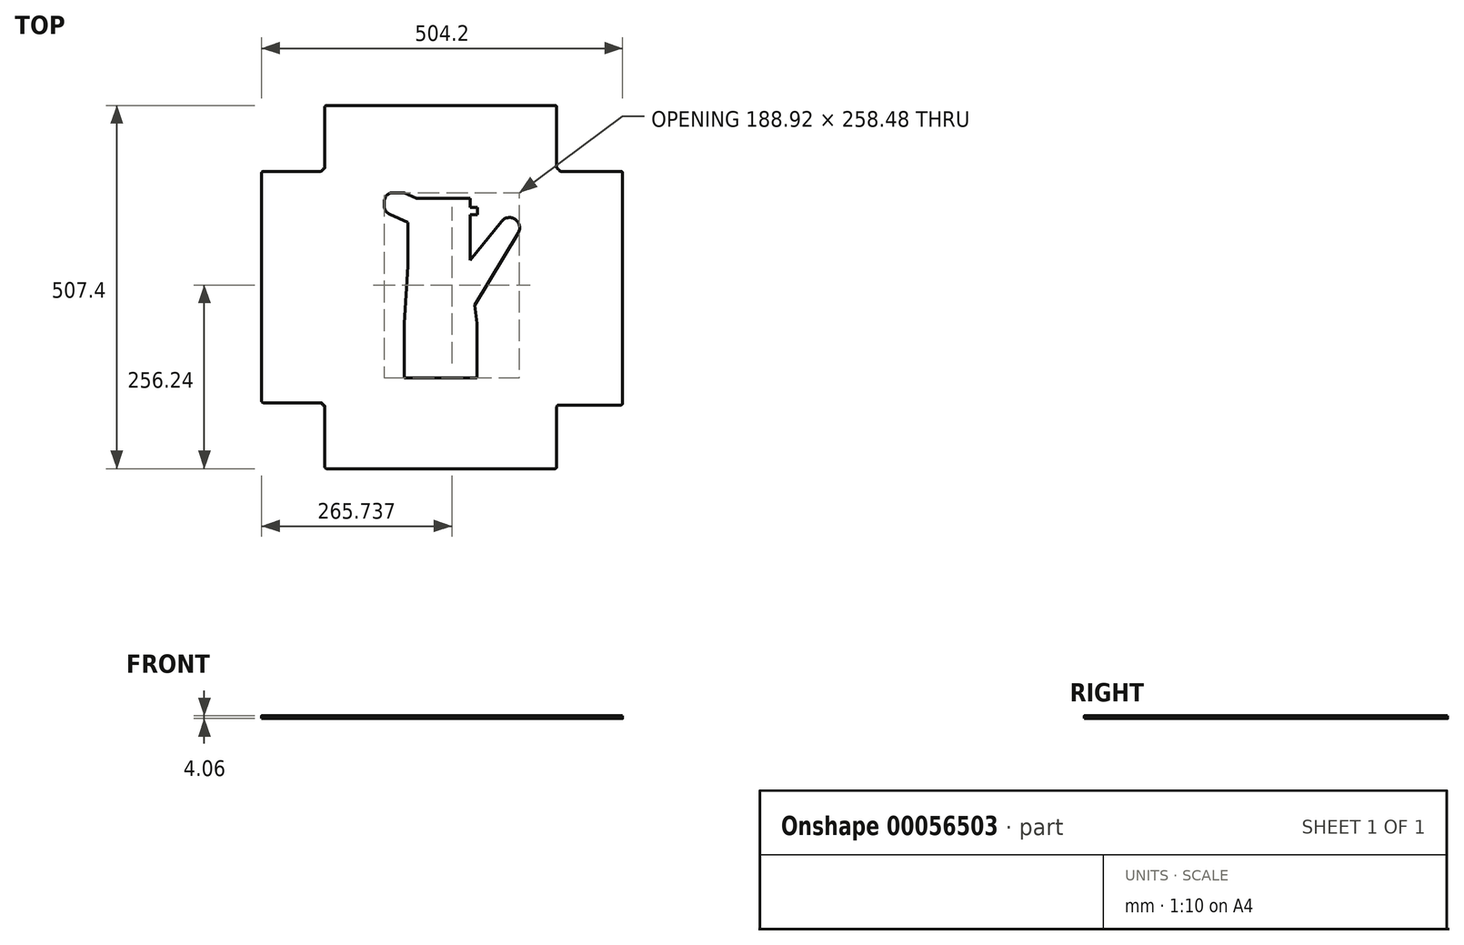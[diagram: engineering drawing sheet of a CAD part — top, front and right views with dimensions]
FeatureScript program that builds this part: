
annotation { "Feature Type Name" : "Feature", "Feature Type Description" : "" }
export const myFeature = defineFeature(function(context is Context, id is Id, definition is map)
    precondition{}
    {
        {
            var Q0;
            Q0=qCreatedBy(makeId("Top.planeOp"),FACE);
            var sketch = newSketch(context, id + "F0", { "sketchPlane" : qUnion([Q0])});
            skLineSegment(sketch, "E0.bottom", {"start": v(330.93, -0.41) * mm, "end": v(334.17, -0.41) * mm});
            skLineSegment(sketch, "E0.top", {"start": v(0.72, 329.2) * mm, "end": v(1.35, 329.2) * mm});
            skLineSegment(sketch, "E0.left", {"start": v(0.72, 328.56) * mm, "end": v(0.72, 329.2) * mm});
            skLineSegment(sketch, "E0.right", {"start": v(330.93, 328.56) * mm, "end": v(330.93, 329.2) * mm});
            skLineSegment(sketch, "E1.bottom", {"start": v(333.47, 326.02) * mm, "end": v(417.3, 326.02) * mm});
            skLineSegment(sketch, "E1.top", {"start": v(336.71, -0.41) * mm, "end": v(417.3, -0.41) * mm});
            skLineSegment(sketch, "E1.left", {"start": v(334.17, 326.02) * mm, "end": v(334.17, -0.41) * mm});
            skLineSegment(sketch, "E1.right", {"start": v(419.83, 323.48) * mm, "end": v(419.83, 2.13) * mm});
            skLineSegment(sketch, "E2.bottom", {"start": v(3.9, 329.2) * mm, "end": v(327.76, 329.2) * mm});
            skLineSegment(sketch, "E2.top", {"start": v(6.43, 418.1) * mm, "end": v(325.22, 418.1) * mm});
            skLineSegment(sketch, "E2.left", {"start": v(3.9, 331.73) * mm, "end": v(3.9, 415.55) * mm});
            skLineSegment(sketch, "E2.right", {"start": v(327.76, 331.73) * mm, "end": v(327.76, 415.55) * mm});
            skLineSegment(sketch, "E3.bottom", {"start": v(-1.82, 326.02) * mm, "end": v(-81.83, 326.02) * mm});
            skLineSegment(sketch, "E3.top", {"start": v(-1.82, 2.76) * mm, "end": v(-81.83, 2.76) * mm});
            skLineSegment(sketch, "E3.left", {"start": v(0.72, 326.61) * mm, "end": v(0.72, 2.76) * mm});
            skLineSegment(sketch, "E3.right", {"start": v(-84.37, 323.48) * mm, "end": v(-84.37, 5.3) * mm});
            skLineSegment(sketch, "E4.bottom", {"start": v(3.9, -0.41) * mm, "end": v(327.03, -0.41) * mm});
            skLineSegment(sketch, "E4.top", {"start": v(6.43, -89.31) * mm, "end": v(325.22, -89.31) * mm});
            skLineSegment(sketch, "E4.left", {"start": v(3.9, -2.95) * mm, "end": v(3.9, -86.77) * mm});
            skLineSegment(sketch, "E4.right", {"start": v(327.76, -3.59) * mm, "end": v(327.76, -86.77) * mm});
            skPoint(sketch, "E5.newPointA", {"position": v(0.72, -0.41) * mm});
            skPoint(sketch, "E5.newPointB", {"position": v(4.53, 326.02) * mm});
            skArc(sketch, "E5.filletArc", {"start": v(-1.82, 326.02) * mm, "mid": v(-0.03, 326.76) * mm, "end": v(0.72, 328.56) * mm});
            skPoint(sketch, "E6.newPointA", {"position": v(330.92, 329.2) * mm});
            skPoint(sketch, "E6.newPointB", {"position": v(3.9, 329.2) * mm});
            skArc(sketch, "E6.filletArc", {"start": v(1.35, 329.2) * mm, "mid": v(3.15, 329.93) * mm, "end": v(3.9, 331.73) * mm});
            skLineSegment(sketch, "E7", {"start": v(330.3, 329.2) * mm, "end": v(330.93, 329.2) * mm});
            skPoint(sketch, "E8.visualSharp", {"position": v(327.76, 329.2) * mm});
            skArc(sketch, "E8.filletArc", {"start": v(327.76, 331.73) * mm, "mid": v(328.5, 329.93) * mm, "end": v(330.3, 329.2) * mm});
            skPoint(sketch, "E9.newPointA", {"position": v(330.93, -1) * mm});
            skPoint(sketch, "E9.newPointB", {"position": v(330.93, 326.02) * mm});
            skArc(sketch, "E9.filletArc", {"start": v(330.93, 328.56) * mm, "mid": v(331.68, 326.76) * mm, "end": v(333.47, 326.02) * mm});
            skLineSegment(sketch, "E10", {"start": v(334.17, -0.41) * mm, "end": v(334.17, -0.41) * mm});
            skPoint(sketch, "E11.visualSharp", {"position": v(334.17, -0.41) * mm});
            skArc(sketch, "E12.filletArc", {"start": v(330.93, -0.41) * mm, "mid": v(328.69, -1.34) * mm, "end": v(327.76, -3.59) * mm});
            skLineSegment(sketch, "E13", {"start": v(0.72, 0.22) * mm, "end": v(0.72, -0.41) * mm});
            skLineSegment(sketch, "E14", {"start": v(0.72, -0.41) * mm, "end": v(1.35, -0.41) * mm});
            skPoint(sketch, "E15.visualSharp", {"position": v(0.72, 2.76) * mm});
            skArc(sketch, "E15.filletArc", {"start": v(0.72, 0.22) * mm, "mid": v(-0.03, 2.02) * mm, "end": v(-1.82, 2.76) * mm});
            skPoint(sketch, "E16.visualSharp", {"position": v(3.9, -0.41) * mm});
            skArc(sketch, "E16.filletArc", {"start": v(3.9, -2.95) * mm, "mid": v(3.15, -1.15) * mm, "end": v(1.35, -0.41) * mm});
            skLineSegment(sketch, "E17", {"start": v(115.02, 37.69) * mm, "end": v(216.62, 37.69) * mm});
            skLineSegment(sketch, "E18", {"start": v(216.62, 37.69) * mm, "end": v(216.62, 113.89) * mm});
            skLineSegment(sketch, "E19", {"start": v(216.62, 113.89) * mm, "end": v(213.52, 139.1) * mm});
            skLineSegment(sketch, "E20", {"start": v(213.52, 139.1) * mm, "end": v(274.03, 239.8) * mm});
            skArc(sketch, "E21", {"start": v(273.96, 239.68) * mm, "mid": v(269.96, 258.79) * mm, "end": v(250.64, 256.08) * mm});
            skLineSegment(sketch, "E22", {"start": v(250.64, 256.08) * mm, "end": v(206.72, 201.76) * mm});
            skLineSegment(sketch, "E23", {"start": v(206.72, 201.76) * mm, "end": v(206.72, 265.26) * mm});
            skLineSegment(sketch, "E24", {"start": v(206.72, 265.26) * mm, "end": v(216.88, 265.26) * mm});
            skLineSegment(sketch, "E25", {"start": v(216.88, 265.26) * mm, "end": v(216.88, 275.42) * mm});
            skLineSegment(sketch, "E26", {"start": v(216.88, 275.42) * mm, "end": v(206.72, 275.42) * mm});
            skLineSegment(sketch, "E27", {"start": v(206.72, 275.42) * mm, "end": v(206.72, 288.12) * mm});
            skLineSegment(sketch, "E28", {"start": v(206.72, 288.12) * mm, "end": v(132.11, 288.12) * mm});
            skLineSegment(sketch, "E29", {"start": v(132.11, 288.12) * mm, "end": v(114.85, 296.17) * mm});
            skLineSegment(sketch, "E30", {"start": v(114.85, 296.17) * mm, "end": v(99.6, 296.17) * mm});
            skArc(sketch, "E31", {"start": v(99.6, 296.17) * mm, "mid": v(90.63, 292.45) * mm, "end": v(86.9, 283.47) * mm});
            skLineSegment(sketch, "E32", {"start": v(119.79, 254.29) * mm, "end": v(119.79, 193.9) * mm});
            skLineSegment(sketch, "E33", {"start": v(115.02, 37.69) * mm, "end": v(115.02, 113.89) * mm});
            skLineSegment(sketch, "E34", {"start": v(119.79, 193.9) * mm, "end": v(115.02, 113.89) * mm});
            skPoint(sketch, "E35.visualSharp", {"position": v(-84.37, 326.02) * mm});
            skArc(sketch, "E35.filletArc", {"start": v(-81.83, 326.02) * mm, "mid": v(-83.63, 325.27) * mm, "end": v(-84.37, 323.48) * mm});
            skPoint(sketch, "E36.visualSharp", {"position": v(-84.37, 2.76) * mm});
            skArc(sketch, "E36.filletArc", {"start": v(-84.37, 5.3) * mm, "mid": v(-83.63, 3.5) * mm, "end": v(-81.83, 2.76) * mm});
            skPoint(sketch, "E37.visualSharp", {"position": v(3.9, -89.31) * mm});
            skArc(sketch, "E37.filletArc", {"start": v(3.9, -86.77) * mm, "mid": v(4.64, -88.57) * mm, "end": v(6.43, -89.31) * mm});
            skPoint(sketch, "E38.visualSharp", {"position": v(327.76, -89.31) * mm});
            skArc(sketch, "E38.filletArc", {"start": v(325.22, -89.31) * mm, "mid": v(327.01, -88.57) * mm, "end": v(327.76, -86.77) * mm});
            skPoint(sketch, "E39.visualSharp", {"position": v(419.83, -0.41) * mm});
            skArc(sketch, "E39.filletArc", {"start": v(417.3, -0.41) * mm, "mid": v(419.09, 0.33) * mm, "end": v(419.83, 2.13) * mm});
            skPoint(sketch, "E40.visualSharp", {"position": v(419.83, 326.02) * mm});
            skArc(sketch, "E40.filletArc", {"start": v(419.83, 323.48) * mm, "mid": v(419.09, 325.27) * mm, "end": v(417.3, 326.02) * mm});
            skPoint(sketch, "E41.visualSharp", {"position": v(327.76, 418.1) * mm});
            skArc(sketch, "E41.filletArc", {"start": v(327.76, 415.55) * mm, "mid": v(327.01, 417.35) * mm, "end": v(325.22, 418.1) * mm});
            skPoint(sketch, "E42.visualSharp", {"position": v(3.9, 418.1) * mm});
            skArc(sketch, "E42.filletArc", {"start": v(6.43, 418.1) * mm, "mid": v(4.64, 417.35) * mm, "end": v(3.9, 415.55) * mm});
            skLineSegment(sketch, "E43", {"start": v(86.9, 277.71) * mm, "end": v(86.9, 283.47) * mm});
            skPoint(sketch, "E44.visualSharp", {"position": v(86.9, 259.93) * mm});
            skArc(sketch, "E44.filletArc", {"start": v(86.9, 277.71) * mm, "mid": v(88.9, 270.89) * mm, "end": v(94.24, 266.2) * mm});
            skLineSegment(sketch, "E45", {"start": v(94.24, 266.2) * mm, "end": v(119.79, 254.29) * mm});
            skLineSegment(sketch, "E46", {"start": v(336.71, -0.41) * mm, "end": v(334.17, -0.41) * mm});
            skSolve(sketch);
        }
        {
            var Q0;
            Q0=makeQuery(id+"F0.imprint","IMPRINT",FACE,{"disambiguationData":[TD([[makeQuery(id+"F0.imprint","IMPRINT",EDGE,{"derivedFrom":sQuery(id+"F0.wireOp",EDGE,"E0.bottom")}),1.0]])]});
            var Q1;
            Q1=makeQuery(id+"F0.imprint","IMPRINT",FACE,{"disambiguationData":[TD([[makeQuery(id+"F0.imprint","IMPRINT",EDGE,{"derivedFrom":sQuery(id+"F0.wireOp",EDGE,"E1.top")}),1.0]])]});
            extrude(context, id + "F1", {"entities" : qUnion([Q0, Q1]), "depth" : 4.06 * mm});
        }
    });
